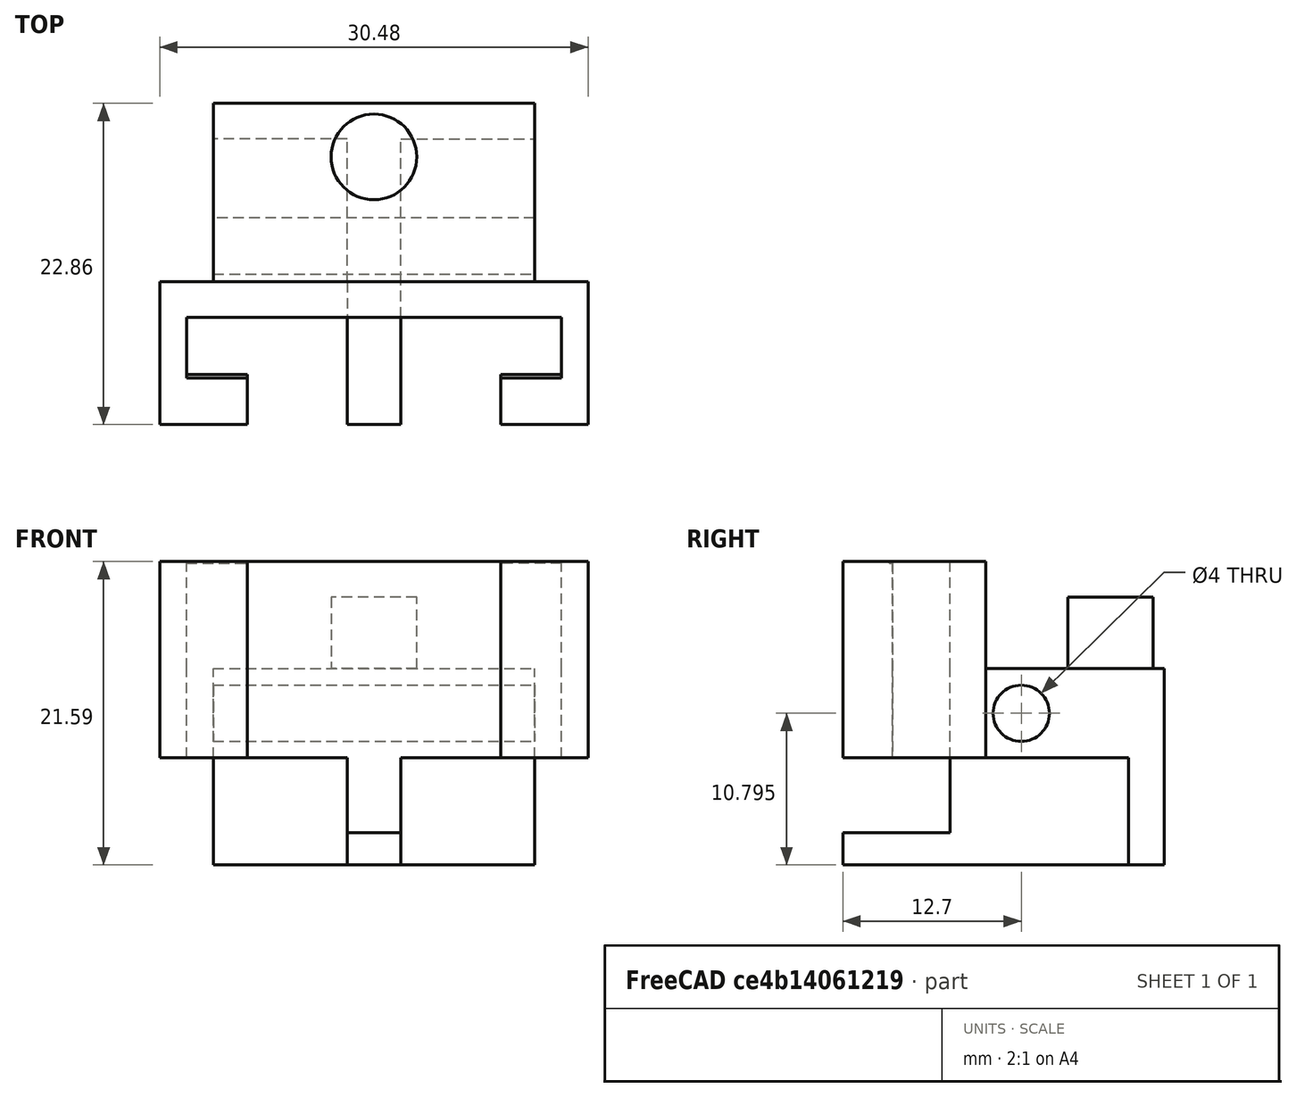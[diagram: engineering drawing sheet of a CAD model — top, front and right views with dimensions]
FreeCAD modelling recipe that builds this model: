
FCSTD DOCUMENT  (FreeCAD 0.18.1R)
Label: nerf_dart_carriage_test_rev_03
License: All rights reserved
LicenseURL: http://en.wikipedia.org/wiki/All_rights_reserved
objects: Sketcher::SketchObject×12, PartDesign::Pad×9, PartDesign::Pocket×2, PartDesign::Body×1, Mesh::Feature×1
note: 35 computed .brp shape members not serialized (recipe doc carries the construction recipe); baked Part::Feature solids carry a one-line shape summary decoded from their .brp

FEATURE [Sketcher::SketchObject] Sketch
  MapMode = 5
  Support = -> [XY_Plane]
  sketch-geometry (12):
    g0: LineSegment StartX=-9.017 StartY=0 StartZ=0 EndX=-9.017 EndY=3.302 EndZ=0
    g1: LineSegment StartX=-9.017 StartY=0 StartZ=0 EndX=-15.24 EndY=0 EndZ=0
    g2: LineSegment StartX=-15.24 StartY=0 StartZ=0 EndX=-15.24 EndY=10.16 EndZ=0
    g3: LineSegment StartX=-15.24 StartY=10.16 StartZ=0 EndX=15.24 EndY=10.16 EndZ=0
    g4: LineSegment StartX=15.24 StartY=10.16 StartZ=0 EndX=15.24 EndY=0 EndZ=0
    g5: LineSegment StartX=15.24 StartY=0 StartZ=0 EndX=9.017 EndY=0 EndZ=0
    g6: LineSegment StartX=9.017 StartY=0 StartZ=0 EndX=9.017 EndY=3.302 EndZ=0
    g7: LineSegment StartX=9.017 StartY=3.302 StartZ=0 EndX=13.335 EndY=3.302 EndZ=0
    g8: LineSegment StartX=13.335 StartY=3.302 StartZ=0 EndX=13.335 EndY=7.62 EndZ=0
    g9: LineSegment StartX=13.335 StartY=7.62 StartZ=0 EndX=-13.335 EndY=7.62 EndZ=0
    g10: LineSegment StartX=-13.335 StartY=7.62 StartZ=0 EndX=-13.335 EndY=3.302 EndZ=0
    g11: LineSegment StartX=-13.335 StartY=3.302 StartZ=0 EndX=-9.017 EndY=3.302 EndZ=0
  constraints (36):
    c: PointOnObject(g0,g-1)
    c: Vertical(g0)
    c: Coincident(g1,g0)
    c: PointOnObject(g1,g-1)
    c: Coincident(g2,g1)
    c: Vertical(g2)
    c: Coincident(g3,g2)
    c: Horizontal(g3)
    c: Coincident(g4,g3)
    c: PointOnObject(g4,g-1)
    c: Vertical(g4)
    c: Coincident(g5,g4)
    c: Horizontal(g5)
    c: Coincident(g6,g5)
    c: Vertical(g6)
    c: Coincident(g7,g6)
    c: Horizontal(g7)
    c: Coincident(g8,g7)
    c: Vertical(g8)
    c: Coincident(g9,g8)
    c: Horizontal(g9)
    c: Coincident(g10,g9)
    c: Vertical(g10)
    c: Coincident(g11,g10)
    c: Coincident(g11,g0)
    c: Horizontal(g11)
    c: DistanceX(g9,g9) = 26.67
    c: DistanceX(g7,g7) = 4.318
    c: Distance(g-1,g0) = 9.017
    c: DistanceX(g3,g3) = 30.48
    c: DistanceY(g6,g6) = 3.302
    c: DistanceY(g0,g0) = 3.302
    c: Distance(g8) = 4.318
    c: Distance(g9,g3) = 2.54
    c: DistanceX(g11,g11) = 4.318
    c: Distance(g9,g2) = 1.905
FEATURE [PartDesign::Pad] Pad
  Length = 6.35
  Length2 = 100.076
  Profile = -> Sketch
  Type = 0
FEATURE [Sketcher::SketchObject] Sketch002
  MapMode = 5
  Placement = pos=(0,0,0) rot=(1,0,0;3.14159rad)
  Support = -> [Pad]
  sketch-geometry (5):
    g0: LineSegment StartX=0 StartY=-7.62 StartZ=0 EndX=1.905 EndY=-7.62 EndZ=0
    g1: LineSegment StartX=1.905 StartY=-7.62 StartZ=0 EndX=1.905 EndY=-10.16 EndZ=0
    g2: LineSegment StartX=1.905 StartY=-10.16 StartZ=0 EndX=-1.905 EndY=-10.16 EndZ=0
    g3: LineSegment StartX=-1.905 StartY=-10.16 StartZ=0 EndX=-1.905 EndY=-7.62 EndZ=0
    g4: LineSegment StartX=-1.905 StartY=-7.62 StartZ=0 EndX=0 EndY=-7.62 EndZ=0
  constraints (15):
    c: PointOnObject(g0,g-2)
    c: Horizontal(g0)
    c: Coincident(g1,g0)
    c: Vertical(g1)
    c: Coincident(g2,g1)
    c: Horizontal(g2)
    c: Coincident(g3,g2)
    c: Vertical(g3)
    c: Coincident(g4,g3)
    c: Coincident(g4,g0)
    c: Horizontal(g4)
    c: Distance(g-1,g0) = 7.62
    c: DistanceX(g2,g2) = 3.81
    c: DistanceX(g4,g4) = 1.905
    c: DistanceY(g1,g1) = 2.54
FEATURE [PartDesign::Pad] Pad001
  BaseFeature = -> Pad
  Length = 7.62
  Length2 = 100.076
  Profile = -> Sketch002
  Type = 0
FEATURE [Sketcher::SketchObject] Sketch003
  MapMode = 5
  Placement = pos=(0,0,-7.62) rot=(1,0,0;3.14159rad)
  Support = -> [Pad001]
  sketch-geometry (6):
    g0: LineSegment StartX=0 StartY=0 StartZ=0 EndX=1.905 EndY=0 EndZ=0
    g1: LineSegment StartX=1.905 StartY=0 StartZ=0 EndX=1.905 EndY=-7.62 EndZ=0
    g2: LineSegment StartX=1.905 StartY=-7.62 StartZ=0 EndX=0 EndY=-7.62 EndZ=0
    g3: LineSegment StartX=0 StartY=-7.62 StartZ=0 EndX=-1.905 EndY=-7.62 EndZ=0
    g4: LineSegment StartX=-1.905 StartY=-7.62 StartZ=0 EndX=-1.905 EndY=0 EndZ=0
    g5: LineSegment StartX=-1.905 StartY=0 StartZ=0 EndX=0 EndY=0 EndZ=0
  constraints (18):
    c: Coincident(g0,g-1)
    c: PointOnObject(g0,g-1)
    c: Vertical(g1)
    c: Coincident(g2,g1)
    c: PointOnObject(g2,g-2)
    c: Horizontal(g2)
    c: Coincident(g3,g2)
    c: Horizontal(g3)
    c: Coincident(g4,g3)
    c: PointOnObject(g4,g-1)
    c: Vertical(g4)
    c: Coincident(g5,g4)
    c: Coincident(g5,g0)
    c: DistanceX(g0,g0) = 1.905
    c: Distance(g3,g1) = 3.81
    c: Distance(g0,g2) = 7.62
    c: DistanceX(g5,g5) = 1.905
    c: DistanceY(g1,g1) = 7.62
FEATURE [PartDesign::Pad] Pad002
  BaseFeature = -> Pad001
  Length = 2.286
  Length2 = 100.076
  Profile = -> Sketch003
  Reversed = true
  Type = 0
FEATURE [Sketcher::SketchObject] Sketch004
  MapMode = 5
  Placement = pos=(0,10.16,0) rot=(0,0.707107,0.707107;3.14159rad)
  Support = -> [Pad002]
  sketch-geometry (5):
    g0: LineSegment StartX=0 StartY=0 StartZ=0 EndX=-27.94 EndY=0 EndZ=0
    g1: LineSegment StartX=-27.94 StartY=0 StartZ=0 EndX=-27.94 EndY=6.35 EndZ=0
    g2: LineSegment StartX=-27.94 StartY=6.35 StartZ=0 EndX=27.94 EndY=6.35 EndZ=0
    g3: LineSegment StartX=27.94 StartY=6.35 StartZ=0 EndX=27.94 EndY=0 EndZ=0
    g4: LineSegment StartX=27.94 StartY=0 StartZ=0 EndX=0 EndY=0 EndZ=0
  constraints (14):
    c: Coincident(g0,g-1)
    c: PointOnObject(g0,g-1)
    c: Coincident(g1,g0)
    c: Vertical(g1)
    c: Coincident(g2,g1)
    c: Horizontal(g2)
    c: Coincident(g3,g2)
    c: PointOnObject(g3,g-1)
    c: Coincident(g4,g3)
    c: Coincident(g4,g0)
    c: Distance(g1) = 6.35
    c: Distance(g2) = 55.88
    c: Vertical(g3)
    c: Distance(g4) = 27.94
FEATURE [PartDesign::Pad] Pad003
  BaseFeature = -> Pad002
  Length = 12.7
  Length2 = 100.076
  Profile = -> Sketch004
  Type = 0
FEATURE [Sketcher::SketchObject] Sketch006
  MapMode = 5
  Placement = pos=(0,0,2e-15) rot=(1,0,0;3.14159rad)
  sketch-geometry (8):
    g0: LineSegment StartX=-27.94 StartY=-10.16 StartZ=0 EndX=-27.94 EndY=-22.86 EndZ=0
    g1: LineSegment StartX=-27.94 StartY=-22.86 StartZ=0 EndX=-11.43 EndY=-22.86 EndZ=0
    g2: LineSegment StartX=-11.43 StartY=-22.86 StartZ=0 EndX=-11.43 EndY=-10.16 EndZ=0
    g3: LineSegment StartX=-11.43 StartY=-10.16 StartZ=0 EndX=-27.94 EndY=-10.16 EndZ=0
    g4: LineSegment StartX=27.94 StartY=-22.86 StartZ=0 EndX=11.43 EndY=-22.86 EndZ=0
    g5: LineSegment StartX=11.43 StartY=-22.86 StartZ=0 EndX=11.43 EndY=-10.16 EndZ=0
    g6: LineSegment StartX=11.43 StartY=-10.16 StartZ=0 EndX=27.94 EndY=-10.16 EndZ=0
    g7: LineSegment StartX=27.94 StartY=-10.16 StartZ=0 EndX=27.94 EndY=-22.86 EndZ=0
  constraints (24):
    c: Vertical(g0)
    c: Coincident(g1,g0)
    c: Horizontal(g1)
    c: Coincident(g2,g1)
    c: Coincident(g3,g2)
    c: Coincident(g3,g0)
    c: Horizontal(g4)
    c: Coincident(g5,g4)
    c: Vertical(g5)
    c: Coincident(g6,g5)
    c: Horizontal(g6)
    c: Coincident(g7,g6)
    c: Coincident(g7,g4)
    c: Vertical(g7)
    c: Distance(g0,g-2) = 27.94
    c: Distance(g6,g-2) = 27.94
    c: DistanceY(g0,g0) = 12.7
    c: DistanceY(g7,g7) = 12.7
    c: Horizontal(g3)
    c: DistanceX(g3,g3) = 16.51
    c: Vertical(g2)
    c: Distance(g6) = 16.51
    c: Distance(g0,g-1) = 10.16
    c: Distance(g6,g-1) = 10.16
FEATURE [PartDesign::Pocket] Pocket
  BaseFeature = -> Pad003
  Length = 30.48
  Length2 = 100.076
  Profile = -> Sketch006
  Type = 0
FEATURE [Sketcher::SketchObject] Sketch007
  MapMode = 5
  Placement = pos=(11.43,0,0) rot=(0.57735,0.57735,0.57735;2.0944rad)
  Support = -> [Pocket]
  sketch-geometry (1):
    g0: Circle CenterX=12.7 CenterY=3.175 CenterZ=0 NormalX=0 NormalY=0 NormalZ=1 AngleXU=0 Radius=2
  constraints (3):
    c: Radius(g0) = 2
    c: Distance(g0,g-1) = 3.175
    c: Distance(g0,g-2) = 12.7
FEATURE [PartDesign::Pocket] Pocket001
  BaseFeature = -> Pocket
  Length = 25.4
  Length2 = 100.076
  Profile = -> Sketch007
  Type = 0
FEATURE [Sketcher::SketchObject] Sketch008
  MapMode = 5
  Placement = pos=(0,1.4e-15,6.35) rot=(0,0,1;0rad)
  Support = -> [Pocket001]
  sketch-geometry (1):
    g0: Circle CenterX=0 CenterY=19.05 CenterZ=0 NormalX=0 NormalY=0 NormalZ=1 AngleXU=0 Radius=3.048
  constraints (3):
    c: PointOnObject(g0,g-2)
    c: Radius(g0) = 3.048
    c: Distance(g-1,g0) = 19.05
FEATURE [PartDesign::Pad] Pad004
  BaseFeature = -> Pocket001
  Length = 5.08
  Length2 = 100.076
  Profile = -> Sketch008
  Type = 0
FEATURE [Sketcher::SketchObject] Sketch009
  MapMode = 5
  Placement = pos=(0,10.16,0) rot=(0,0.707107,0.707107;3.14159rad)
  Support = -> [Pad004]
  sketch-geometry (5):
    g0: LineSegment StartX=0 StartY=0 StartZ=0 EndX=1.905 EndY=0 EndZ=0
    g1: LineSegment StartX=1.905 StartY=0 StartZ=0 EndX=1.905 EndY=-7.62 EndZ=0
    g2: LineSegment StartX=1.905 StartY=-7.62 StartZ=0 EndX=-1.905 EndY=-7.62 EndZ=0
    g3: LineSegment StartX=-1.905 StartY=-7.62 StartZ=0 EndX=-1.905 EndY=0 EndZ=0
    g4: LineSegment StartX=-1.905 StartY=0 StartZ=0 EndX=0 EndY=0 EndZ=0
  constraints (14):
    c: Coincident(g0,g-1)
    c: Coincident(g1,g0)
    c: Vertical(g1)
    c: Coincident(g2,g1)
    c: Horizontal(g2)
    c: Coincident(g3,g2)
    c: Vertical(g3)
    c: Coincident(g4,g3)
    c: Coincident(g4,g0)
    c: Horizontal(g4)
    c: Horizontal(g0)
    c: DistanceX(g2,g2) = 3.81
    c: DistanceX(g0,g0) = 1.905
    c: DistanceY(g1,g1) = 7.62
FEATURE [PartDesign::Pad] Pad005
  BaseFeature = -> Pad004
  Length = 10.16
  Length2 = 100.076
  Profile = -> Sketch009
  Type = 0
FEATURE [Sketcher::SketchObject] Sketch010
  MapMode = 5
  Placement = pos=(0,20.32,-4.7e-15) rot=(0,0.707107,0.707107;3.14159rad)
  Support = -> [Pad005]
  sketch-geometry (5):
    g0: LineSegment StartX=0 StartY=0 StartZ=0 EndX=11.43 EndY=0 EndZ=0
    g1: LineSegment StartX=11.43 StartY=0 StartZ=0 EndX=11.43 EndY=-7.62 EndZ=0
    g2: LineSegment StartX=11.43 StartY=-7.62 StartZ=0 EndX=-11.43 EndY=-7.62 EndZ=0
    g3: LineSegment StartX=-11.43 StartY=-7.62 StartZ=0 EndX=-11.43 EndY=0 EndZ=0
    g4: LineSegment StartX=-11.43 StartY=0 StartZ=0 EndX=0 EndY=0 EndZ=0
  constraints (14):
    c: Coincident(g0,g-1)
    c: Horizontal(g0)
    c: Coincident(g1,g0)
    c: Vertical(g1)
    c: Coincident(g2,g1)
    c: Horizontal(g2)
    c: Coincident(g3,g2)
    c: PointOnObject(g3,g-1)
    c: Coincident(g4,g3)
    c: Coincident(g4,g0)
    c: Vertical(g3)
    c: DistanceY(g1,g1) = 7.62
    c: DistanceX(g2,g2) = 22.86
    c: DistanceX(g0,g0) = 11.43
FEATURE [PartDesign::Pad] Pad006
  BaseFeature = -> Pad005
  Length = 2.54
  Length2 = 100.076
  Profile = -> Sketch010
  Type = 0
FEATURE [Sketcher::SketchObject] Sketch011
  MapMode = 5
  Placement = pos=(0,0,6.35) rot=(0,0,1;0rad)
  Support = -> [Pad006]
FEATURE [Sketcher::SketchObject] Sketch012
  MapMode = 5
  Placement = pos=(0,0,6.35) rot=(0,0,1;0rad)
  Support = -> [Pad006]
  sketch-geometry (30):
    g0: LineSegment StartX=-9.017 StartY=0 StartZ=0 EndX=-9.017 EndY=3.302 EndZ=0
    g1: LineSegment StartX=-15.24 StartY=3.302 StartZ=0 EndX=-15.24 EndY=0 EndZ=0
    g2: LineSegment StartX=-15.24 StartY=0 StartZ=0 EndX=-9.017 EndY=0 EndZ=0
    g3: LineSegment StartX=9.017 StartY=0 StartZ=0 EndX=9.017 EndY=3.302 EndZ=0
    g4: LineSegment StartX=15.24 StartY=3.302 StartZ=0 EndX=15.24 EndY=0 EndZ=0
    g5: LineSegment StartX=15.24 StartY=0 StartZ=0 EndX=9.017 EndY=0 EndZ=0
    g6: LineSegment StartX=-15.24 StartY=10.16 StartZ=0 EndX=15.24 EndY=10.16 EndZ=0
    g7: LineSegment StartX=15.24 StartY=10.16 StartZ=0 EndX=15.24 EndY=7.747 EndZ=0
    g8: LineSegment StartX=-15.24 StartY=7.747 StartZ=0 EndX=-15.24 EndY=10.16 EndZ=0
    g9: LineSegment StartX=-15.24 StartY=3.302 StartZ=0 EndX=-15.24 EndY=7.747 EndZ=0
    g10: LineSegment StartX=15.24 StartY=3.302 StartZ=0 EndX=15.24 EndY=7.747 EndZ=0
    g11: LineSegment StartX=9.017 StartY=3.302 StartZ=0 EndX=13.335 EndY=3.302 EndZ=0
    g12: LineSegment StartX=13.335 StartY=3.302 StartZ=0 EndX=13.335 EndY=7.62 EndZ=0
    g13: LineSegment StartX=-9.017 StartY=3.302 StartZ=0 EndX=-13.335 EndY=3.302 EndZ=0
    g14: LineSegment StartX=-13.335 StartY=3.302 StartZ=0 EndX=-13.335 EndY=7.62 EndZ=0
    g15: LineSegment StartX=-13.335 StartY=7.62 StartZ=0 EndX=13.335 EndY=7.62 EndZ=0
    g16: GeomPoint X=15.24 Y=3.302 Z=0
    g17: GeomPoint X=15.24 Y=3.302 Z=0
    g18: GeomPoint X=15.24 Y=3.302 Z=0
    g19: GeomPoint X=15.24 Y=3.302 Z=0
    g20: GeomPoint X=15.24 Y=3.302 Z=0
    g21: GeomPoint X=15.24 Y=3.302 Z=0
    g22: GeomPoint X=15.24 Y=3.302 Z=0
    g23: GeomPoint X=15.24 Y=3.302 Z=0
    g24: GeomPoint X=-15.24 Y=3.302 Z=0
    g25: GeomPoint X=-15.24 Y=3.302 Z=0
    g26: GeomPoint X=-15.24 Y=3.302 Z=0
    g27: GeomPoint X=-15.24 Y=3.302 Z=0
    g28: GeomPoint X=-15.24 Y=3.302 Z=0
    g29: GeomPoint X=-15.24 Y=3.302 Z=0
  constraints (61):
    c: PointOnObject(g0,g-1)
    c: Vertical(g0)
    c: PointOnObject(g1,g-1)
    c: Coincident(g2,g1)
    c: Coincident(g2,g0)
    c: PointOnObject(g3,g-1)
    c: Vertical(g3)
    c: PointOnObject(g4,g-1)
    c: Vertical(g4)
    c: Coincident(g5,g4)
    c: Coincident(g5,g3)
    c: Horizontal(g6)
    c: Coincident(g7,g6)
    c: Vertical(g7)
    c: Coincident(g8,g6)
    c: Vertical(g8)
    c: Distance(g0) = 3.302
    c: Distance(g3) = 3.302
    c: Distance(g0,g-1) = 9.017
    c: Distance(g3,g-1) = 9.017
    c: Parallel(g1,g8)
    c: Distance(g8,g-2) = 15.24
    c: Coincident(g10,g7)
    c: Distance(g5) = 6.223
    c: Coincident(g11,g3)
    c: Horizontal(g11)
    c: DistanceX(g6,g6) = 30.48
    c: Distance(g11,g4) = 1.905
    c: Coincident(g12,g11)
    c: Vertical(g12)
    c: Distance(g2) = 6.223
    c: Coincident(g13,g0)
    c: Horizontal(g13)
    c: Coincident(g14,g13)
    c: Vertical(g14)
    c: Distance(g1,g13) = 1.905
    c: Coincident(g15,g14)
    c: Coincident(g15,g12)
    c: Horizontal(g15)
    c: Distance(g14) = 4.318
    c: Distance(g7) = 2.413
    c: Distance(g4) = 3.302
    c: Distance(g1) = 3.302
    c: Coincident(g16,g4)
    c: Coincident(g17,g4)
    c: Coincident(g18,g10)
    c: Coincident(g19,g10)
    c: Coincident(g20,g4)
    c: Coincident(g21,g10)
    c: Coincident(g22,g4)
    c: Coincident(g23,g10)
    c: Coincident(g8,g9)
    c: Coincident(g24,g9)
    c: Coincident(g26,g9)
    c: Coincident(g27,g1)
    c: Coincident(g28,g9)
    c: Coincident(g29,g1)
    c: Coincident(g1,g9)
    c: Coincident(g10,g4)
    c: Distance(g-1,g6) = 10.16
    c: Distance(g8) = 2.413
FEATURE [PartDesign::Pad] Pad007
  BaseFeature = -> Pad006
  Length = 7.62
  Length2 = 100.076
  Profile = -> Sketch012
  Type = 0
FEATURE [Sketcher::SketchObject] Sketch013
  MapMode = 5
  Placement = pos=(0,3.302,0) rot=(0,0.707107,0.707107;3.14159rad)
  Support = -> [Pad007]
  sketch-geometry (8):
    g0: LineSegment StartX=9.017 StartY=0 StartZ=0 EndX=13.335 EndY=0 EndZ=0
    g1: LineSegment StartX=13.335 StartY=0 StartZ=0 EndX=13.335 EndY=13.843 EndZ=0
    g2: LineSegment StartX=13.335 StartY=13.843 StartZ=0 EndX=9.017 EndY=13.843 EndZ=0
    g3: LineSegment StartX=9.017 StartY=13.843 StartZ=0 EndX=9.017 EndY=0 EndZ=0
    g4: LineSegment StartX=-9.017 StartY=0 StartZ=0 EndX=-13.335 EndY=0 EndZ=0
    g5: LineSegment StartX=-13.335 StartY=0 StartZ=0 EndX=-13.335 EndY=13.843 EndZ=0
    g6: LineSegment StartX=-13.335 StartY=13.843 StartZ=0 EndX=-9.017 EndY=13.843 EndZ=0
    g7: LineSegment StartX=-9.017 StartY=13.843 StartZ=0 EndX=-9.017 EndY=0 EndZ=0
  constraints (24):
    c: Coincident(g0,g1)
    c: Coincident(g1,g2)
    c: Coincident(g2,g3)
    c: Coincident(g3,g0)
    c: Horizontal(g0)
    c: Horizontal(g2)
    c: Vertical(g1)
    c: Vertical(g3)
    c: PointOnObject(g0,g-1)
    c: Coincident(g4,g5)
    c: Coincident(g5,g6)
    c: Coincident(g6,g7)
    c: Coincident(g7,g4)
    c: Horizontal(g4)
    c: Horizontal(g6)
    c: Vertical(g5)
    c: Vertical(g7)
    c: PointOnObject(g4,g-1)
    c: Distance(g-1,g0) = 9.017
    c: Distance(g-1,g7) = 9.017
    c: Distance(g0) = 4.318
    c: Distance(g4) = 4.318
    c: Distance(g7) = 13.843
    c: Distance(g3) = 13.843
FEATURE [PartDesign::Pad] Pad008
  BaseFeature = -> Pad007
  Length = 0.254
  Length2 = 100.076
  Profile = -> Sketch013
  Type = 0
FEATURE [PartDesign::Body] Body
  Group = -> [Sketch,Pad,Sketch002,Pad001,Sketch003,Pad002,Sketch004,Pad003,Sketch006,Pocket,Sketch007,Pocket001,Sketch008,Pad004,Sketch009,Pad005,Sketch010,Pad006,Sketch011,Sketch012,Pad007,Sketch013,Pad008]
  Origin = -> Origin
  Tip = -> Pad008
FEATURE [Mesh::Feature] Mesh  label="Pad008 (Meshed)"
